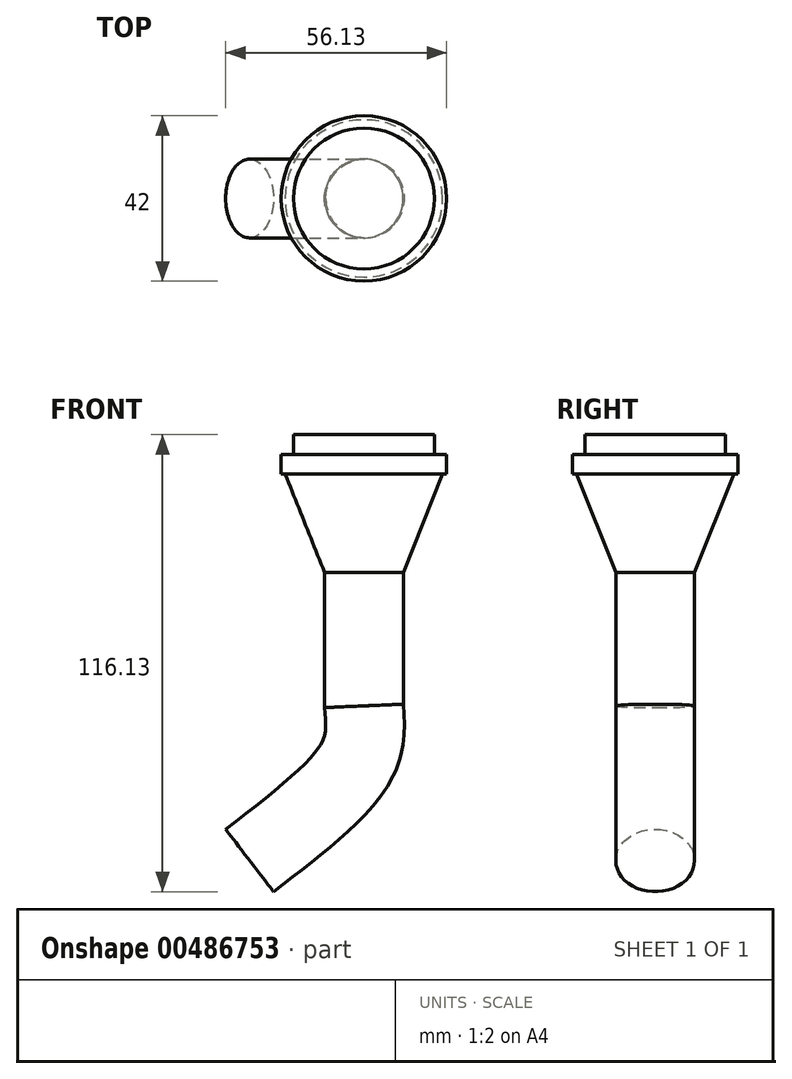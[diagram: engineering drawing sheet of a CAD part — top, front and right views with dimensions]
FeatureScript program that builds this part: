
annotation { "Feature Type Name" : "Feature", "Feature Type Description" : "" }
export const myFeature = defineFeature(function(context is Context, id is Id, definition is map)
    precondition{}
    {
        {
            var Q0;
            Q0=qCreatedBy(makeId("Top.planeOp"),FACE);
            var sketch = newSketch(context, id + "F0", { "sketchPlane" : qUnion([Q0])});
            skCircle(sketch, "E0", {"center": v(0, 0) * mm, "radius": 21 * mm});
            skCircle(sketch, "E1", {"center": v(0, 0) * mm, "radius": 17.9 * mm});
            skSolve(sketch);
        }
        {
            var Q0;
            Q0 = qSketchRegion(id + "F0", true);
            var Q1;
            Q1=makeQuery(id+"F0.imprint","IMPRINT",FACE,{"disambiguationData":[TD([[makeQuery(id+"F0.imprint","IMPRINT",EDGE,{"derivedFrom":sQuery(id+"F0.wireOp",EDGE,"E1")}),1.0]])]});
            extrude(context, id + "F1", {"entities" : qUnion([Q0, Q1]), "depth" : 5 * mm, "offsetDistance" : 25 * mm});
        }
        {
            var Q0;
            Q0=makeQuery(id+"F1.opExtrude","CAP_FACE",FACE,{"disambiguationData":[OSD([sQuery(id+"F0.wireOp",EDGE,"E0")])],"isStart":false});
            var sketch = newSketch(context, id + "F2", { "sketchPlane" : qUnion([Q0])});
            skCircle(sketch, "E2", {"center": v(0, 0) * mm, "radius": 17.9 * mm});
            skSolve(sketch);
        }
        {
            var Q0;
            Q0 = qSketchRegion(id + "F2", true);
            extrude(context, id + "F3", {"entities" : qUnion([Q0]), "operationType" : NewBodyOperationType.ADD, "depth" : 5 * mm, "offsetDistance" : 25 * mm});
        }
        {
            var Q0;
            Q0=makeQuery(id+"F1.opExtrude","CAP_FACE",FACE,{"disambiguationData":[OSD([sQuery(id+"F0.wireOp",EDGE,"E0")])],"isStart":true});
            var sketch = newSketch(context, id + "F4", { "sketchPlane" : qUnion([Q0])});
            skCircle(sketch, "E3", {"center": v(0, 0) * mm, "radius": 20 * mm});
            skSolve(sketch);
        }
        {
            var Q0;
            Q0=makeQuery(id+"F4.imprint","IMPRINT",FACE,{"disambiguationData":[TD([[makeQuery(id+"F4.imprint","IMPRINT",EDGE,{"derivedFrom":sQuery(id+"F4.wireOp",EDGE,"E3")}),-1.0]])]});
            cPlane(context, id + "F5", {"entities" : qUnion([Q0]), "cplaneType" : CPlaneType.OFFSET, "offset" : 25 * mm, "width" : 150 * mm, "height" : 150 * mm});
        }
        {
            var Q0;
            Q0=qCreatedBy(id+"F5.planeOp",FACE);
            var sketch = newSketch(context, id + "F6", { "sketchPlane" : qUnion([Q0])});
            skCircle(sketch, "E4", {"center": v(0, 0) * mm, "radius": 10 * mm});
            skSolve(sketch);
        }
        {
            var Q0;
            Q0 = qSketchRegion(id + "F6", true);
            extrude(context, id + "F7", {"entities" : qUnion([Q0]), "depth" : 25 * mm, "offsetDistance" : 25 * mm});
        }
        {
            var Q0;
            Q0=makeQuery(id+"F4.imprint","IMPRINT",FACE,{"disambiguationData":[TD([[makeQuery(id+"F4.imprint","IMPRINT",EDGE,{"derivedFrom":sQuery(id+"F4.wireOp",EDGE,"E3")}),1.0]])]});
            var Q1;
            Q1=makeQuery(id+"F7.opExtrude","CAP_FACE",FACE,{"disambiguationData":[OSD([sQuery(id+"F6.wireOp",EDGE,"E4")])],"isStart":true});
            loft(context, id + "F8", {"sheetProfilesArray" : [{ "sheetProfileEntities" : qUnion([Q0]) }, { "sheetProfileEntities" : qUnion([Q1]) }]});
        }
        {
            var Q0;
            Q0=qCreatedBy(makeId("Front.planeOp"),FACE);
            var sketch = newSketch(context, id + "F9", { "sketchPlane" : qUnion([Q0])});
            skLineSegment(sketch, "E5.0", {"start": v(10, -50) * mm, "end": v(-10, -50) * mm});
            skLineSegment(sketch, "E6", {"start": v(0, -50) * mm, "end": v(0, -58.92) * mm});
            skFitSpline(sketch, "E7", {"points": [v(0, -58.92) * mm, v(0, -67.57) * mm, v(-5.17, -77.72) * mm, v(-29.04, -98.2) * mm], "startDerivative": vector(2.98, -35.22) * mm, "endDerivative": vector(-59.82, -46.01) * mm});
            skSolve(sketch);
        }
        {
            var Q0;
            Q0=makeQuery(id+"F7.opExtrude","CAP_FACE",FACE,{"disambiguationData":[OSD([sQuery(id+"F6.wireOp",EDGE,"E4")])],"isStart":false});
            var Q1;
            Q1=sQuery(id+"F9.wireOp",EDGE,"E6");
            var Q2;
            Q2=sQuery(id+"F9.wireOp",EDGE,"E7");
            sweep(context, id + "F10", {"operationType" : NewBodyOperationType.ADD, "profiles" : qUnion([Q0]), "path" : qUnion([Q1, Q2])});
        }
    });
